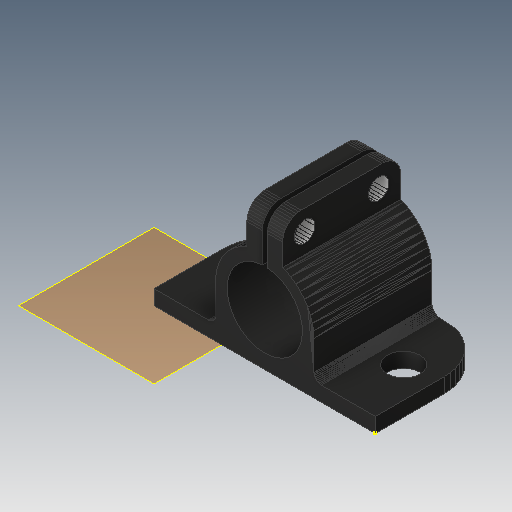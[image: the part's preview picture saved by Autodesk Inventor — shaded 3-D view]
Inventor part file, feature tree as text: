
AUTODESK INVENTOR PART (.ipt)
format: ipt  version: 2017 (Build 210142000, 142)  size: 718,848 bytes
history: native  units: mm
features: sketch x6, other x3, plane x2, hole x1, projected_geometry x1
ambient origin geometry x8: Origin, YZ Plane, XZ Plane, XY Plane, X Axis, Y Axis, Z Axis, Center Point
bodies: Solid1 (feature_tree)
feature tree (13):
  other  "12mmrodholder_CPY.ipt"
  hole  "Hole1"  [1 undecoded]
  other  "Solid1::12mmrodholder_CPY.ipt"
  other  "TaggingFeature1"
  sketch  "Sketch2"  dims[d0=10.0mm]
  sketch  "Sketch3"  dims[d1=3.3mm d2=6.0mm d3=4.0mm d4=2.0mm d5=90.0deg d6=8.0mm d7=20.594885mm]
  sketch  "Sketch4"
  sketch  "Sketch5"
  sketch  "Sketch6"
  plane  "Work Plane1"
  plane  "Work Plane2"
  sketch  "Sketch7"
  projected_geometry  "Projected Loop1"
note: 1 required parameter value undecoded (feature->parameter linkage not recoverable at this tier; creation-order binding heuristic only, values carry confidence <= 0.55)
